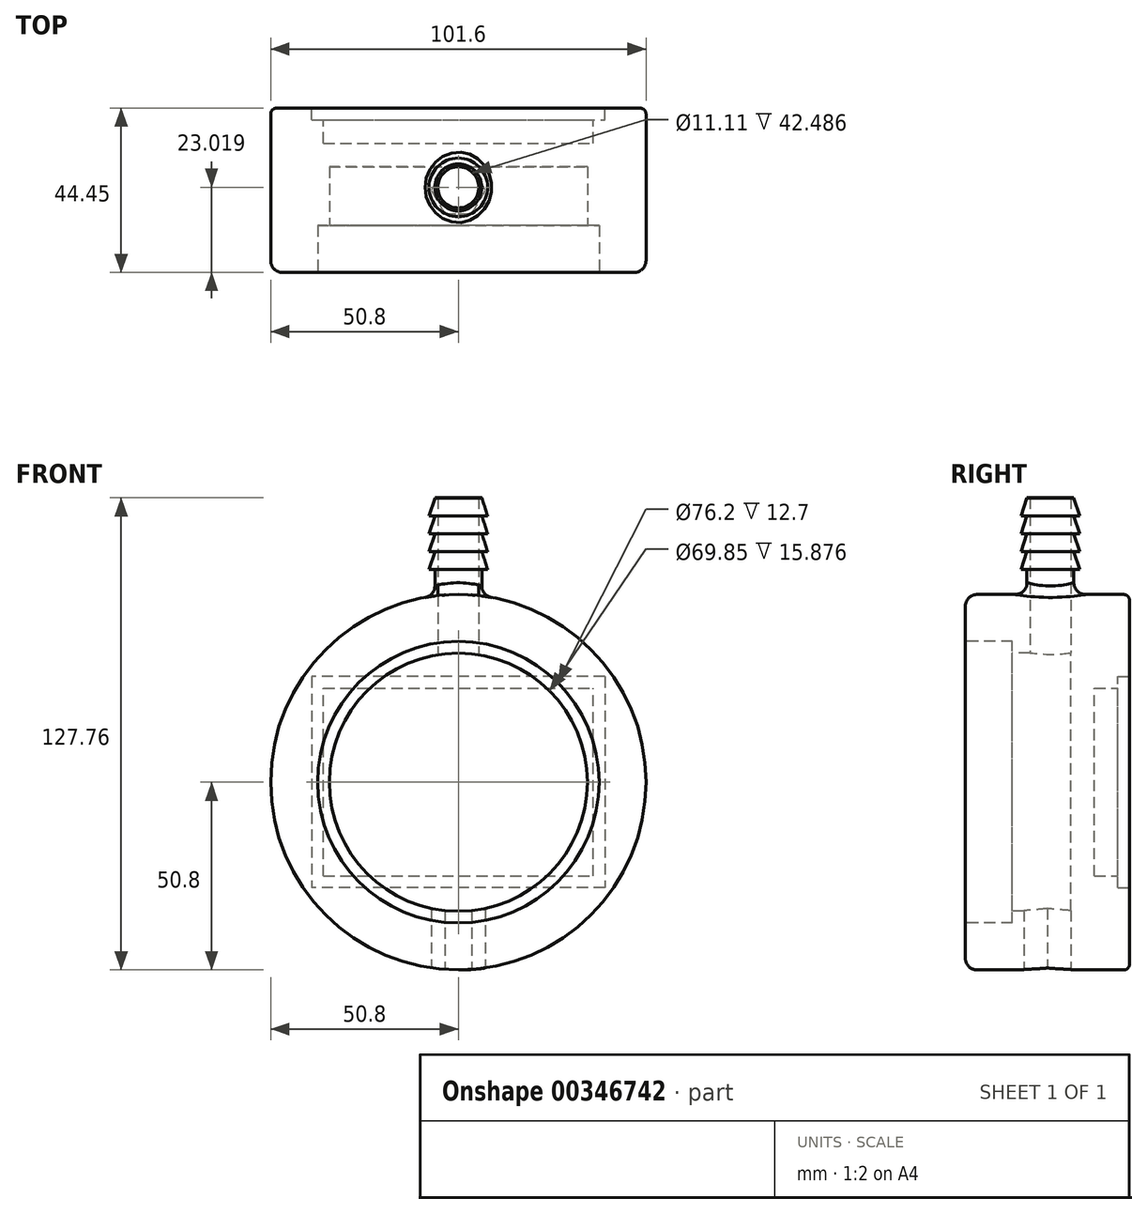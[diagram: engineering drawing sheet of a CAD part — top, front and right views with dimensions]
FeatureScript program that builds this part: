
annotation { "Feature Type Name" : "Feature", "Feature Type Description" : "" }
export const myFeature = defineFeature(function(context is Context, id is Id, definition is map)
    precondition{}
    {
        {
            var Q0;
            Q0=qCreatedBy(makeId("Front.planeOp"),FACE);
            var sketch = newSketch(context, id + "F0", { "sketchPlane" : qUnion([Q0])});
            skCircle(sketch, "E0", {"center": v(0, 0) * mm, "radius": 50.8 * mm});
            skSolve(sketch);
        }
        {
            var Q0;
            Q0 = qSketchRegion(id + "F0", true);
            extrude(context, id + "F1", {"entities" : qUnion([Q0]), "oppositeDirection" : true, "depth" : 44.45 * mm});
        }
        {
            var Q0;
            Q0=qCreatedBy(makeId("Front.planeOp"),FACE);
            var sketch = newSketch(context, id + "F2", { "sketchPlane" : qUnion([Q0])});
            skCircle(sketch, "E1", {"center": v(0, 0) * mm, "radius": 34.93 * mm});
            skSolve(sketch);
        }
        {
            var Q0;
            Q0=makeQuery(id+"F2.imprint","IMPRINT",FACE,{"disambiguationData":[TD([[makeQuery(id+"F2.imprint","IMPRINT",EDGE,{"derivedFrom":sQuery(id+"F2.wireOp",EDGE,"E1")}),1.0]])]});
            var Q1;
            Q1=sQuery(id+"F2.wireOp",EDGE,"E1");
            extrude(context, id + "F3", {"entities" : qUnion([Q0]), "operationType" : NewBodyOperationType.REMOVE, "surfaceEntities" : qUnion([Q1]), "oppositeDirection" : true, "depth" : 28.57 * mm});
        }
        {
            var Q0;
            Q0=qCreatedBy(makeId("Front.planeOp"),FACE);
            var sketch = newSketch(context, id + "F4", { "sketchPlane" : qUnion([Q0])});
            skCircle(sketch, "E2", {"center": v(0, 0) * mm, "radius": 38.1 * mm});
            skSolve(sketch);
        }
        {
            var Q0;
            Q0 = qSketchRegion(id + "F4", true);
            extrude(context, id + "F5", {"entities" : qUnion([Q0]), "operationType" : NewBodyOperationType.REMOVE, "oppositeDirection" : true, "depth" : 12.7 * mm});
        }
        {
            var Q0;
            Q0=qCreatedBy(makeId("Top.planeOp"),FACE);
            cPlane(context, id + "F6", {"entities" : qUnion([Q0]), "cplaneType" : CPlaneType.OFFSET, "offset" : 50.8 * mm, "width" : 152.4 * mm, "height" : 152.4 * mm});
        }
        {
            var Q0;
            Q0=qCreatedBy(makeId("Front.planeOp"),FACE);
            cPlane(context, id + "F7", {"entities" : qUnion([Q0]), "cplaneType" : CPlaneType.OFFSET, "offset" : 44.45 * mm, "oppositeDirection" : true, "width" : 152.4 * mm, "height" : 152.4 * mm});
        }
        {
            var Q0;
            Q0=makeQuery(id+"F1.opExtrude","CAP_EDGE",EDGE,{"disambiguationData":[OSD([sQuery(id+"F0.wireOp",EDGE,"E0")])],"isStart":true});
            fillet(context, id + "F8", {"entities" : qUnion([Q0]), "radius" : 3.17 * mm, "tangentPropagation" : true, "allowEdgeOverflow" : false});
        }
        {
            var Q0;
            Q0=makeQuery(id+"F1.opExtrude","CAP_EDGE",EDGE,{"disambiguationData":[OSD([sQuery(id+"F0.wireOp",EDGE,"E0")])],"isStart":false});
            fillet(context, id + "F9", {"entities" : qUnion([Q0]), "radius" : 1.59 * mm, "tangentPropagation" : true, "allowEdgeOverflow" : false});
        }
        {
            var Q0;
            Q0=qCreatedBy(makeId("Top.planeOp"),FACE);
            cPlane(context, id + "F10", {"entities" : qUnion([Q0]), "cplaneType" : CPlaneType.OFFSET, "offset" : 50.8 * mm, "oppositeDirection" : true, "width" : 152.4 * mm, "height" : 152.4 * mm});
        }
        {
            var Q0;
            Q0=qCreatedBy(id+"F10.planeOp",FACE);
            var sketch = newSketch(context, id + "F11", { "sketchPlane" : qUnion([Q0])});
            skLineSegment(sketch, "E3", {"start": v(-50.8, 3.17) * mm, "end": v(-50.8, 42.86) * mm});
            skLineSegment(sketch, "E4", {"start": v(50.8, 42.86) * mm, "end": v(50.8, 3.17) * mm});
            skCircle(sketch, "E5.0", {"center": v(0, 22.23) * mm, "radius": 6.35 * mm});
            skCircle(sketch, "E6.cCircle", {"center": v(0, 22.23) * mm, "radius": 6.35 * mm, "construction": true});
            skLineSegment(sketch, "E6.0", {"start": v(3.67, 28.57) * mm, "end": v(7.33, 22.23) * mm});
            skLineSegment(sketch, "E6.1", {"start": v(7.33, 22.23) * mm, "end": v(3.67, 15.88) * mm});
            skLineSegment(sketch, "E6.2", {"start": v(3.67, 15.88) * mm, "end": v(-3.67, 15.88) * mm});
            skLineSegment(sketch, "E6.3", {"start": v(-3.67, 15.88) * mm, "end": v(-7.33, 22.23) * mm});
            skLineSegment(sketch, "E6.4", {"start": v(-7.33, 22.22) * mm, "end": v(-3.67, 28.57) * mm});
            skLineSegment(sketch, "E6.5", {"start": v(-3.67, 28.57) * mm, "end": v(3.67, 28.57) * mm});
            skPoint(sketch, "E6.0.midPoint", {"position": v(5.5, 25.4) * mm});
            skSolve(sketch);
        }
        {
            var Q0;
            {var subQ0=sQuery(id+"F11.wireOp",EDGE,"E5.0");var subQ4=makeQuery(id+"F11.imprint","INTERSECT",VERTEX,{"derivedFrom":[subQ0,sQuery(id+"F11.wireOp",EDGE,"E6.5")]});Q0=makeQuery(id+"F11.imprint","IMPRINT",FACE,{"disambiguationData":[TD([[makeQuery(id+"F11.imprint","IMPRINT",EDGE,{"disambiguationData":[TD([[subQ4,1.0]])],"derivedFrom":subQ0}),1.0]])]});}
            var Q1;
            {var subQ0=sQuery(id+"F11.wireOp",EDGE,"E6.5");var subQ1=sQuery(id+"F11.wireOp",EDGE,"E5.0");var subQ2=makeQuery(id+"F11.imprint","INTERSECT",VERTEX,{"derivedFrom":[subQ1,subQ0]});Q1=makeQuery(id+"F11.imprint","IMPRINT",FACE,{"disambiguationData":[TD([[makeQuery(id+"F11.imprint","IMPRINT",EDGE,{"disambiguationData":[TD([[subQ2,1.0]])],"derivedFrom":subQ1}),-1.0]])]});}
            var Q2;
            {var subQ0=sQuery(id+"F11.wireOp",EDGE,"E6.5");var subQ1=sQuery(id+"F11.wireOp",EDGE,"E5.0");var subQ2=makeQuery(id+"F11.imprint","INTERSECT",VERTEX,{"derivedFrom":[subQ1,subQ0]});Q2=makeQuery(id+"F11.imprint","IMPRINT",FACE,{"disambiguationData":[TD([[makeQuery(id+"F11.imprint","IMPRINT",EDGE,{"disambiguationData":[TD([[subQ2,-1.0]])],"derivedFrom":subQ1}),-1.0]])]});}
            var Q3;
            {var subQ0=sQuery(id+"F11.wireOp",EDGE,"E6.4");var subQ1=sQuery(id+"F11.wireOp",EDGE,"E5.0");var subQ2=makeQuery(id+"F11.imprint","INTERSECT",VERTEX,{"derivedFrom":[subQ1,subQ0]});Q3=makeQuery(id+"F11.imprint","IMPRINT",FACE,{"disambiguationData":[TD([[makeQuery(id+"F11.imprint","IMPRINT",EDGE,{"disambiguationData":[TD([[subQ2,-1.0]])],"derivedFrom":subQ1}),-1.0]])]});}
            var Q4;
            {var subQ0=sQuery(id+"F11.wireOp",EDGE,"E6.3");var subQ1=sQuery(id+"F11.wireOp",EDGE,"E5.0");var subQ2=makeQuery(id+"F11.imprint","INTERSECT",VERTEX,{"derivedFrom":[subQ1,subQ0]});Q4=makeQuery(id+"F11.imprint","IMPRINT",FACE,{"disambiguationData":[TD([[makeQuery(id+"F11.imprint","IMPRINT",EDGE,{"disambiguationData":[TD([[subQ2,-1.0]])],"derivedFrom":subQ1}),-1.0]])]});}
            var Q5;
            {var subQ0=sQuery(id+"F11.wireOp",EDGE,"E6.2");var subQ1=sQuery(id+"F11.wireOp",EDGE,"E5.0");var subQ2=makeQuery(id+"F11.imprint","INTERSECT",VERTEX,{"derivedFrom":[subQ1,subQ0]});Q5=makeQuery(id+"F11.imprint","IMPRINT",FACE,{"disambiguationData":[TD([[makeQuery(id+"F11.imprint","IMPRINT",EDGE,{"disambiguationData":[TD([[subQ2,-1.0]])],"derivedFrom":subQ1}),-1.0]])]});}
            var Q6;
            {var subQ0=sQuery(id+"F11.wireOp",EDGE,"E6.0");var subQ1=sQuery(id+"F11.wireOp",EDGE,"E5.0");var subQ2=makeQuery(id+"F11.imprint","INTERSECT",VERTEX,{"derivedFrom":[subQ1,subQ0]});Q6=makeQuery(id+"F11.imprint","IMPRINT",FACE,{"disambiguationData":[TD([[makeQuery(id+"F11.imprint","IMPRINT",EDGE,{"disambiguationData":[TD([[subQ2,1.0]])],"derivedFrom":subQ1}),-1.0]])]});}
            extrude(context, id + "F12", {"entities" : qUnion([Q0, Q1, Q2, Q3, Q4, Q5, Q6]), "operationType" : NewBodyOperationType.REMOVE, "depth" : 25.4 * mm});
        }
        {
            var Q0;
            Q0=qCreatedBy(id+"F6.planeOp",FACE);
            var sketch = newSketch(context, id + "F13", { "sketchPlane" : qUnion([Q0])});
            skCircle(sketch, "E7.0", {"center": v(0, 23.02) * mm, "radius": 5.56 * mm});
            skSolve(sketch);
        }
        {
            var Q0;
            Q0=makeQuery(id+"F13.imprint","IMPRINT",FACE,{"disambiguationData":[TD([[makeQuery(id+"F13.imprint","IMPRINT",EDGE,{"derivedFrom":sQuery(id+"F13.wireOp",EDGE,"E7.0")}),1.0]])]});
            extrude(context, id + "F14", {"entities" : qUnion([Q0]), "operationType" : NewBodyOperationType.REMOVE, "oppositeDirection" : true, "depth" : 17.46 * mm});
        }
        {
            var Q0;
            Q0=qCreatedBy(id+"F6.planeOp",FACE);
            var sketch = newSketch(context, id + "F15", { "sketchPlane" : qUnion([Q0])});
            skCircle(sketch, "E8.0", {"center": v(0, 23.02) * mm, "radius": 5.56 * mm});
            skCircle(sketch, "E9", {"center": v(0, 23.02) * mm, "radius": 6.35 * mm});
            skSolve(sketch);
        }
        {
            var Q0;
            Q0=makeQuery(id+"F15.imprint","IMPRINT",FACE,{"disambiguationData":[TD([[makeQuery(id+"F15.imprint","IMPRINT",EDGE,{"derivedFrom":sQuery(id+"F15.wireOp",EDGE,"E8.0")}),-1.0]])]});
            extrude(context, id + "F16", {"entities" : qUnion([Q0]), "depth" : 26.67 * mm});
        }
        {
            var Q0;
            Q0=qCreatedBy(makeId("Right.planeOp"),FACE);
            var sketch = newSketch(context, id + "F17", { "sketchPlane" : qUnion([Q0])});
            skLineSegment(sketch, "E10.0", {"start": v(16.67, 77.47) * mm, "end": v(29.37, 77.47) * mm});
            skLineSegment(sketch, "E11", {"start": v(16.67, 76.9) * mm, "end": v(15.08, 72.08) * mm});
            skLineSegment(sketch, "E12", {"start": v(15.08, 72.08) * mm, "end": v(16.67, 72.08) * mm});
            skLineSegment(sketch, "E13", {"start": v(16.67, 72.08) * mm, "end": v(15.08, 67.25) * mm});
            skLineSegment(sketch, "E14", {"start": v(15.08, 67.25) * mm, "end": v(16.67, 67.25) * mm});
            skLineSegment(sketch, "E15", {"start": v(16.67, 67.25) * mm, "end": v(15.08, 62.43) * mm});
            skLineSegment(sketch, "E16", {"start": v(15.08, 62.43) * mm, "end": v(16.67, 62.43) * mm});
            skLineSegment(sketch, "E17", {"start": v(16.67, 62.43) * mm, "end": v(15.08, 57.6) * mm});
            skLineSegment(sketch, "E18", {"start": v(15.08, 57.6) * mm, "end": v(16.67, 57.6) * mm});
            skLineSegment(sketch, "E19", {"start": v(23.02, 77.47) * mm, "end": v(23.02, 52.44) * mm, "construction": true});
            skLineSegment(sketch, "E20.0", {"start": v(17.46, 77.47) * mm, "end": v(28.58, 77.47) * mm});
            skLineSegment(sketch, "E21", {"start": v(16.67, 77.7) * mm, "end": v(16.67, 57.6) * mm});
            skSolve(sketch);
        }
        {
            var Q0;
            Q0=makeQuery(id+"F16.opExtrude","SWEPT_BODY",BODY,{"disambiguationData":[OSD([sQuery(id+"F15.wireOp",EDGE,"E8.0"),sQuery(id+"F15.wireOp",EDGE,"E9")])]});
            transform(context, id + "F18", {"entities" : qUnion([Q0]), "transformType" : TransformType.TRANSLATION_3D, "dx" : 0 * mm, "dy" : 0 * mm, "dz" : -0.5 * mm, "makeCopy" : false});
        }
        {
            var Q0;
            Q0=makeQuery(id+"F16.opExtrude","SWEPT_BODY",BODY,{"disambiguationData":[OSD([sQuery(id+"F15.wireOp",EDGE,"E8.0"),sQuery(id+"F15.wireOp",EDGE,"E9")])]});
            var Q1;
            Q1=makeQuery(id+"F1.opExtrude","SWEPT_BODY",BODY,{"disambiguationData":[OSD([sQuery(id+"F0.wireOp",EDGE,"E0")])]});
            booleanBodies(context, id + "F19", {"operationType" : BooleanOperationType.UNION, "tools" : qUnion([Q0, Q1])});
        }
        {
            var Q0;
            Q0=makeQuery(id+"F19.opBoolean","INTERSECT",EDGE,{"derivedFrom":[makeQuery(id+"F1.opExtrude","SWEPT_FACE",FACE,{"disambiguationData":[OSD([sQuery(id+"F0.wireOp",EDGE,"E0")])]}),makeQuery(id+"F16.opExtrude","SWEPT_FACE",FACE,{"disambiguationData":[OSD([sQuery(id+"F15.wireOp",EDGE,"E9")])]})]});
            fillet(context, id + "F20", {"entities" : qUnion([Q0]), "radius" : 3.17 * mm, "tangentPropagation" : true, "allowEdgeOverflow" : false});
        }
        {
            var Q0;
            {var subQ0=sQuery(id+"F17.wireOp",EDGE,"E13");Q0=makeQuery(id+"F17.imprint","IMPRINT",FACE,{"disambiguationData":[TD([[makeQuery(id+"F17.imprint","IMPRINT",EDGE,{"derivedFrom":subQ0}),1.0]])]});}
            var Q1;
            {var subQ0=sQuery(id+"F17.wireOp",EDGE,"E15");Q1=makeQuery(id+"F17.imprint","IMPRINT",FACE,{"disambiguationData":[TD([[makeQuery(id+"F17.imprint","IMPRINT",EDGE,{"derivedFrom":subQ0}),1.0]])]});}
            var Q2;
            {var subQ0=sQuery(id+"F17.wireOp",EDGE,"E17");Q2=makeQuery(id+"F17.imprint","IMPRINT",FACE,{"disambiguationData":[TD([[makeQuery(id+"F17.imprint","IMPRINT",EDGE,{"derivedFrom":subQ0}),1.0]])]});}
            var Q3;
            {var subQ0=sQuery(id+"F17.wireOp",EDGE,"E11");Q3=makeQuery(id+"F17.imprint","IMPRINT",FACE,{"disambiguationData":[TD([[makeQuery(id+"F17.imprint","IMPRINT",EDGE,{"derivedFrom":subQ0}),1.0]])]});}
            var Q4;
            Q4=sQuery(id+"F17.wireOp",EDGE,"E19");
            revolve(context, id + "F21", {"operationType" : NewBodyOperationType.ADD, "entities" : qUnion([Q0, Q1, Q2, Q3]), "axis" : qUnion([Q4]), "revolveType" : RevolveType.FULL});
        }
        {
            var Q0;
            Q0=qCreatedBy(id+"F7.planeOp",FACE);
            var sketch = newSketch(context, id + "F22", { "sketchPlane" : qUnion([Q0])});
            skCircle(sketch, "E22.0.0", {"center": v(0, 0) * mm, "radius": 49.21 * mm});
            skLineSegment(sketch, "E23.bottom", {"start": v(-39.69, -28.57) * mm, "end": v(39.69, -28.57) * mm});
            skLineSegment(sketch, "E23.top", {"start": v(-39.69, 28.57) * mm, "end": v(39.69, 28.57) * mm});
            skLineSegment(sketch, "E23.left", {"start": v(-39.69, -28.58) * mm, "end": v(-39.69, 28.57) * mm});
            skLineSegment(sketch, "E23.right", {"start": v(39.69, -28.58) * mm, "end": v(39.69, 28.57) * mm});
            skLineSegment(sketch, "E24.bottom", {"start": v(-36.51, -25.4) * mm, "end": v(36.51, -25.4) * mm});
            skLineSegment(sketch, "E24.top", {"start": v(-36.51, 25.4) * mm, "end": v(36.51, 25.4) * mm});
            skLineSegment(sketch, "E24.left", {"start": v(-36.51, -25.4) * mm, "end": v(-36.51, 25.4) * mm});
            skLineSegment(sketch, "E24.right", {"start": v(36.51, -25.4) * mm, "end": v(36.51, 25.4) * mm});
            skSolve(sketch);
        }
        {
            var Q0;
            Q0=makeQuery(id+"F22.imprint","IMPRINT",FACE,{"disambiguationData":[TD([[makeQuery(id+"F22.imprint","IMPRINT",EDGE,{"derivedFrom":sQuery(id+"F22.wireOp",EDGE,"E24.bottom")}),1.0]])]});
            extrude(context, id + "F23", {"entities" : qUnion([Q0]), "operationType" : NewBodyOperationType.REMOVE, "depth" : 9.52 * mm});
        }
        {
            var Q0;
            Q0=makeQuery(id+"F22.imprint","IMPRINT",FACE,{"disambiguationData":[TD([[makeQuery(id+"F22.imprint","IMPRINT",EDGE,{"derivedFrom":sQuery(id+"F22.wireOp",EDGE,"E23.bottom")}),1.0]])]});
            var Q1;
            Q1=sQuery(id+"F22.wireOp",EDGE,"E23.top");
            var Q2;
            Q2=sQuery(id+"F22.wireOp",EDGE,"E23.left");
            var Q3;
            Q3=sQuery(id+"F22.wireOp",EDGE,"E23.bottom");
            var Q4;
            Q4=sQuery(id+"F22.wireOp",EDGE,"E23.right");
            extrude(context, id + "F24", {"entities" : qUnion([Q0]), "operationType" : NewBodyOperationType.REMOVE, "surfaceEntities" : qUnion([Q1, Q2, Q3, Q4]), "depth" : 3.17 * mm, "hasSecondDirection" : true, "secondDirectionOppositeDirection" : true, "secondDirectionDepth" : 25.4 * mm});
        }
    });
